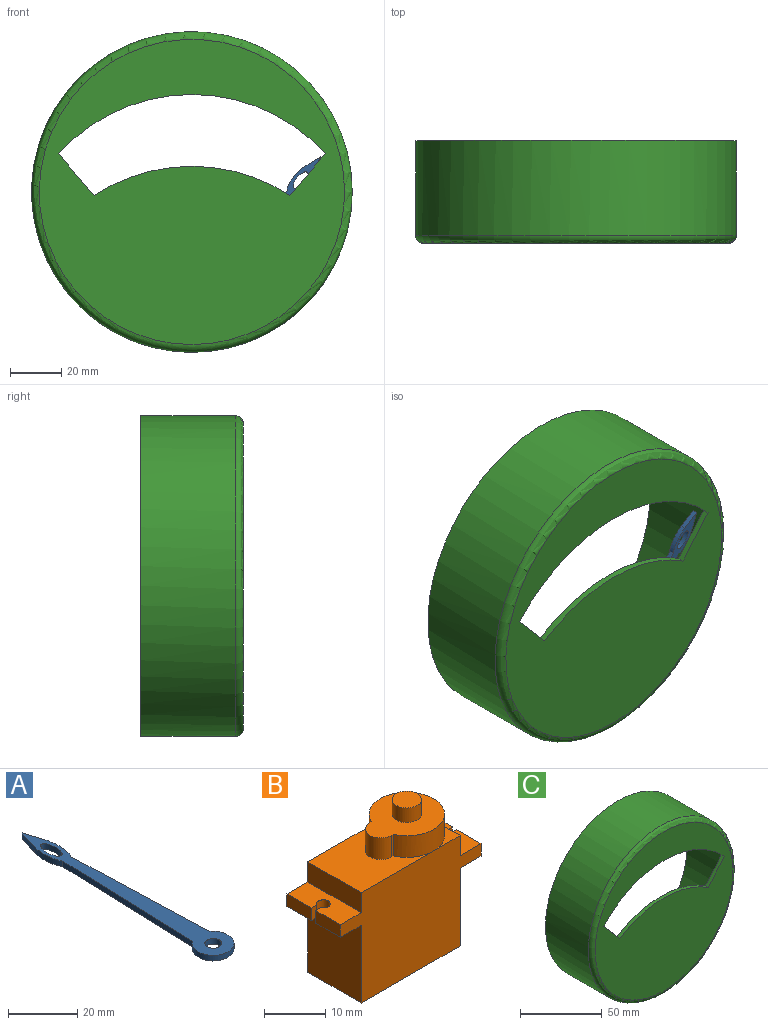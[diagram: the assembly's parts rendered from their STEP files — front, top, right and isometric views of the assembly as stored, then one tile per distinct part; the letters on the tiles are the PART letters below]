
ASSEMBLY  parts=3 mates=3
PART A: 11 faces, bbox 12x84x2 mm
  f0: cylinder r=6mm len=12mm, axis (0,0,-1), area 60.5mm2, adj f1,f6,f9,f10
  f1: plane 54.81x2mm, normal (1,0.03,0), area 109.7mm2, adj f0,f2,f9,f10
  f2: extruded ~11.01x2mm, area 22.6mm2, adj f1,f3,f9,f10
  f3: plane 7.31x2.34mm, normal (0.95,0.3,0), area 15.4mm2, adj f2,f4,f9,f10
  f4: plane 7.31x2.34mm, normal (-0.95,0.3,0), area 15.4mm2, adj f3,f5,f9,f10
  f5: extruded ~11.01x2mm, area 22.6mm2, adj f4,f6,f9,f10
  f6: plane 54.81x2mm, normal (-1,0.03,0), area 109.7mm2, adj f0,f5,f9,f10
  f7: cylinder r=2.4mm len=4.8mm, axis (0,0,-1), area 30.2mm2, adj f9,f10
  f8: extruded ~8x3.5mm, area 37.5mm2, adj f9,f10
  f9: plane 84x12mm, normal (0,0,1), area 424mm2, adj f0,f1,f2,f3,f4,f5,f6,f7
  f10: plane 84x12mm, normal (0,0,-1), area 424mm2, adj f0,f1,f2,f3,f4,f5,f6,f7
PART B: 31 faces, bbox 32.4x12.3x29.2 mm
  f0: plane 6.15x6.15mm, normal (0,0,1), area 8.1mm2, adj f6,f22,f27
  f1: plane 6.15x6.15mm, normal (0,0,1), area 8.1mm2, adj f5,f22,f27
  f2: plane 12.3x4.8mm, normal (0,0,1), area 53.8mm2, adj f5,f6,f15,f16,f17,f18,f19,f21
  f3: plane 15.5x12.3mm, normal (-1,0,0), area 190.6mm2, adj f5,f6,f8,f20
  f4: plane 15.5x12.3mm, normal (1,0,0), area 190.6mm2, adj f5,f6,f8,f14
  f5: plane 32.4x22mm, normal (0,1,0), area 525.6mm2, adj f1,f2,f3,f4,f7,f8,f13,f14
  f6: plane 32.4x22mm, normal (0,-1,0), area 525.6mm2, adj f0,f2,f3,f4,f7,f8,f9,f14
  f7: plane 12.3x4.8mm, normal (0,0,1), area 53.8mm2, adj f5,f6,f9,f10,f11,f12,f13,f22
  f8: plane 22.8x12.3mm, normal (0,0,-1), area 280.4mm2, adj f3,f4,f5,f6
  f9: plane 5.65x2.5mm, normal (1,0,0), area 14.1mm2, adj f6,f7,f10,f14
  f10: plane 2.5x1.16mm, normal (0,1,0), area 2.9mm2, adj f7,f9,f11,f14
  f11: cylinder r=1.15mm len=2.5mm, axis (0,0,1), area 15.5mm2, adj f7,f10,f12,f14
  f12: plane 2.5x1.16mm, normal (0,-1,0), area 2.9mm2, adj f7,f11,f13,f14
  f13: plane 5.65x2.5mm, normal (1,0,0), area 14.1mm2, adj f5,f7,f12,f14
  f14: plane 12.3x4.8mm, normal (0,0,-1), area 53.8mm2, adj f4,f5,f6,f9,f10,f11,f12,f13
  f15: plane 5.65x2.5mm, normal (-1,0,0), area 14.1mm2, adj f2,f6,f19,f20
  f16: plane 5.65x2.5mm, normal (-1,0,0), area 14.1mm2, adj f2,f5,f17,f20
  f17: plane 2.5x1.16mm, normal (0,-1,0), area 2.9mm2, adj f2,f16,f18,f20
  f18: cylinder r=1.15mm len=2.5mm, axis (0,0,1), area 15.5mm2, adj f2,f17,f19,f20
  f19: plane 2.5x1.16mm, normal (0,1,0), area 2.9mm2, adj f2,f15,f18,f20
  f20: plane 12.3x4.8mm, normal (0,0,-1), area 53.8mm2, adj f3,f5,f6,f15,f16,f17,f18,f19
  f21: plane 12.3x4mm, normal (-1,0,0), area 49.2mm2, adj f2,f5,f6,f23
  f22: plane 12.3x4mm, normal (1,0,0), area 49.2mm2, adj f0,f1,f5,f6,f7
  f23: plane 16.65x12.3mm, normal (0,0,1), area 135.4mm2, adj f5,f6,f21,f24,f25,f26,f27
  f24: plane 4.3x0.38mm, normal (0,1,0), area 1.6mm2, adj f23,f25,f27,f28
  f25: cylinder r=2.5mm len=5mm, axis (0,0,-1), area 33.8mm2, adj f23,f24,f26,f28
  f26: plane 4.3x0.38mm, normal (0,-1,0), area 1.6mm2, adj f23,f25,f27,f28
  f27: cylinder r=6.15mm len=12.3mm, axis (0,0,-1), area 144mm2, adj f0,f1,f23,f24,f26,f28
  f28: plane 14.65x12.3mm, normal (0,0,1), area 110.7mm2, adj f24,f25,f26,f27,f29
  f29: cylinder r=2.4mm len=4.8mm, axis (0,0,-1), area 43.7mm2, adj f28,f30
  f30: plane 4.8x4.8mm, normal (0,0,1), area 18.1mm2, adj f29
PART C: 37 faces, bbox 135.3x40x135.3 mm
  f0: plane 119x119mm, normal (0,1,0), area 8476.7mm2, adj f6,f7,f8,f9,f10,f11,f13,f19
  f1: plane 119x119mm, normal (0,-1,0), area 8582.8mm2, adj f4,f7,f8,f9,f10
  f2: cylinder r=62.5mm len=125mm, axis (0,1,0), area 14529.9mm2, adj f3,f4
  f3: plane 125x125mm, normal (0,1,0), area 962.1mm2, adj f2,f5
  f4: torus R=59.5mm, axis (0,-1,0), area 1818.3mm2, adj f1,f2
  f5: cylinder r=60mm len=120mm, axis (0,1,0), area 13948.7mm2, adj f3,f6
  f6: torus R=59.5mm, axis (0,-1,0), area 295.2mm2, adj f0,f5
  f7: cylinder r=70mm len=76.34mm, axis (0,-1,0), area 201.9mm2, adj f0,f1,f8,f9
  f8: plane 16.19x13.83mm, normal (0.76,0,0.65), area 53.2mm2, adj f0,f1,f7,f10
  f9: plane 16.19x13.83mm, normal (-0.76,0,0.65), area 53.2mm2, adj f0,f1,f7,f10
  f10: cylinder r=70mm len=104mm, axis (0,-1,0), area 293.1mm2, adj f0,f1,f8,f9
  f11: cylinder r=2.5mm len=13mm, axis (0,-1,0), area 152.6mm2, adj f0,f12,f19,f20,f21,f22,f23,f24
  f12: plane 5x5mm, normal (0,1,0), area 16.5mm2, adj f11,f17
  f13: cylinder r=2.5mm len=13mm, axis (0,-1,0), area 152.6mm2, adj f0,f14,f28,f29,f30,f31,f32,f33
  f14: plane 5x5mm, normal (0,1,0), area 16.5mm2, adj f13,f15
  f15: cylinder r=1mm len=8mm, axis (0,1,0), area 50.3mm2, adj f14,f16
  f16: plane 2x2mm, normal (0,1,0), area 3.1mm2, adj f15
  f17: cylinder r=1mm len=8mm, axis (0,1,0), area 50.3mm2, adj f12,f18
  f18: plane 2x2mm, normal (0,1,0), area 3.1mm2, adj f17
  f19: plane 8.56x4.94mm, normal (-0.87,0,0.5), area 24.4mm2, adj f0,f11,f21
  f20: plane 8.56x4.94mm, normal (0.87,0,-0.5), area 24.4mm2, adj f0,f11,f21
  f21: plane 8.56x5.94mm, normal (0.42,0.55,0.72), area 20.1mm2, adj f0,f11,f19,f20
  f22: plane 8.56x4.94mm, normal (0.5,0,0.87), area 24.4mm2, adj f0,f11,f24
  f23: plane 8.56x4.94mm, normal (-0.5,0,-0.87), area 24.4mm2, adj f0,f11,f24
  f24: plane 8.56x5.94mm, normal (0.72,0.55,-0.42), area 20.1mm2, adj f0,f11,f22,f23
  f25: plane 8.56x4.94mm, normal (0.87,0,-0.5), area 24.4mm2, adj f0,f11,f27
  f26: plane 8.56x4.94mm, normal (-0.87,0,0.5), area 24.4mm2, adj f0,f11,f27
  f27: plane 8.56x5.94mm, normal (-0.42,0.55,-0.72), area 20.1mm2, adj f0,f11,f25,f26
  f28: plane 8.56x5.71mm, normal (-1,0,0), area 24.4mm2, adj f0,f13,f30
  f29: plane 8.56x5.71mm, normal (1,0,0), area 24.4mm2, adj f0,f13,f30
  f30: plane 8.56x5.71mm, normal (0,0.55,0.83), area 20.1mm2, adj f0,f13,f28,f29
  f31: plane 8.56x5.71mm, normal (0,0,-1), area 24.4mm2, adj f0,f13,f33
  f32: plane 8.56x5.71mm, normal (0,0,1), area 24.4mm2, adj f0,f13,f33
  f33: plane 8.56x5.71mm, normal (-0.83,0.55,0), area 20.1mm2, adj f0,f13,f31,f32
  f34: plane 8.56x5.71mm, normal (1,0,0), area 24.4mm2, adj f0,f13,f36
  f35: plane 8.56x5.71mm, normal (-1,0,0), area 24.4mm2, adj f0,f13,f36
  f36: plane 8.56x5.71mm, normal (0,0.55,-0.83), area 20.1mm2, adj f0,f13,f34,f35
PLACE A rot(axis=(0.89,0.32,-0.32),96.7deg) t=(-38.51,-6.4,-30.51)mm
PLACE B rot(axis=(0.99,0.09,-0.09),90.4deg) t=(-39.27,-6.5,-39.67)mm
PLACE C t=(-21.8,0,9.5)mm
MATE cylindrical B.f11 <-> C.f11  axis (0,1,0) through (-13.19,-22,-38.02)mm
MATE cylindrical A.f0 <-> B.f27  axis (0,-1,0) through (-21.8,-35.7,-36.5)mm
MATE cylindrical B.f18 <-> C.f13  axis (0,-1,0) through (-40.76,-24.5,-33.16)mm
